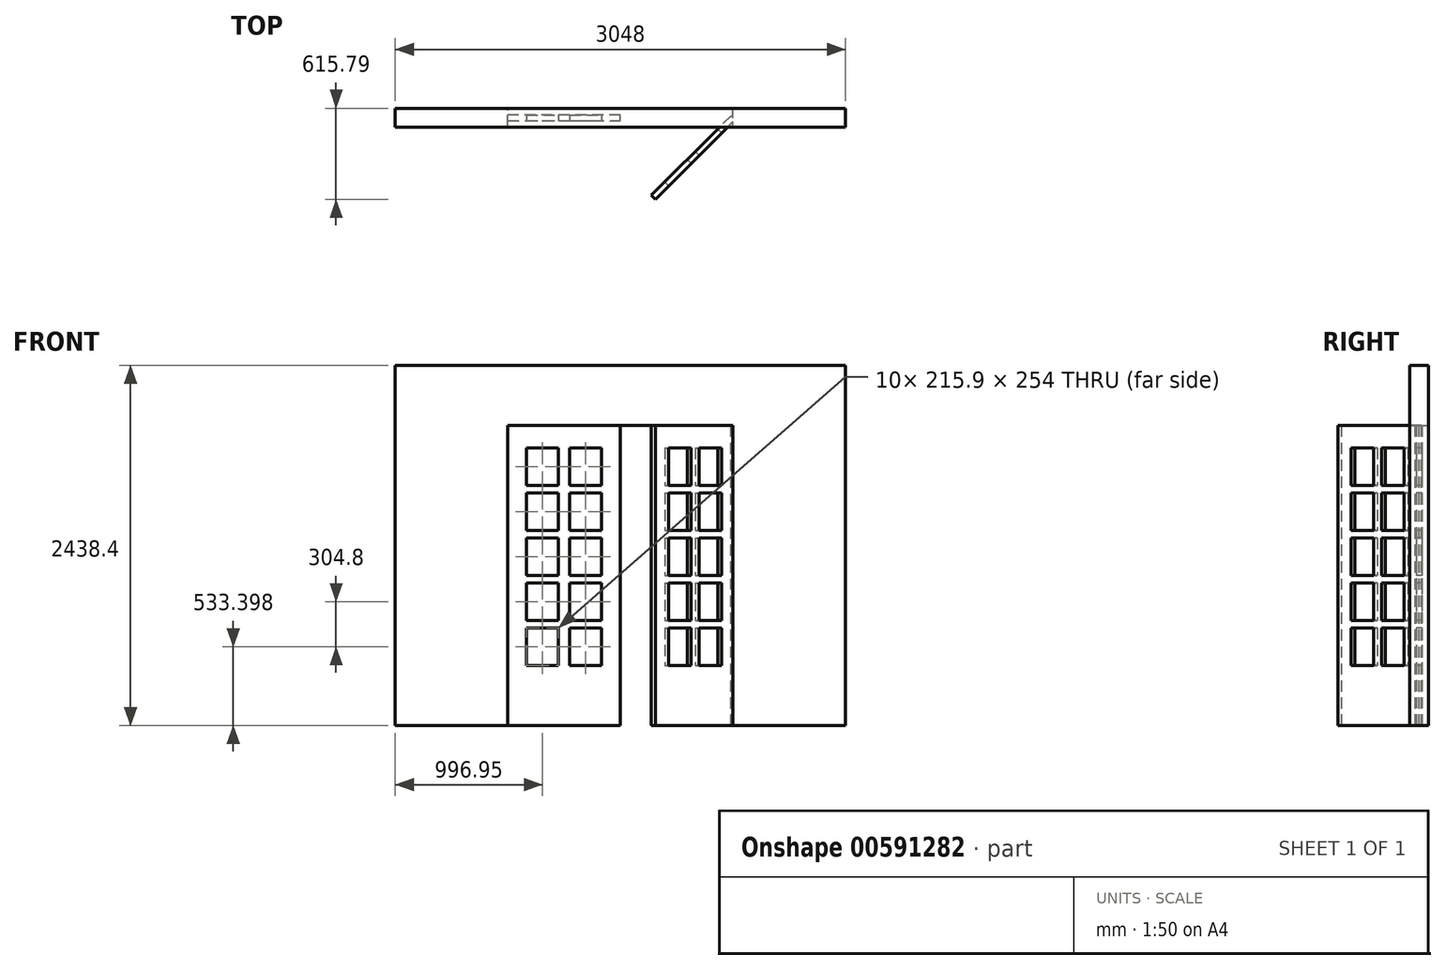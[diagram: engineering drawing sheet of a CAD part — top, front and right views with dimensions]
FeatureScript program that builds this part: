
annotation { "Feature Type Name" : "Feature", "Feature Type Description" : "" }
export const myFeature = defineFeature(function(context is Context, id is Id, definition is map)
    precondition{}
    {
        {
            var Q0;
            Q0=qCreatedBy(makeId("Front.planeOp"),FACE);
            var sketch = newSketch(context, id + "F0", { "sketchPlane" : qUnion([Q0])});
            skLineSegment(sketch, "E0", {"start": v(-2286, -766.6) * mm, "end": v(-1524, -766.6) * mm});
            skLineSegment(sketch, "E1", {"start": v(-1524, -766.6) * mm, "end": v(-1524, 1265.4) * mm});
            skLineSegment(sketch, "E2", {"start": v(-1524, 1265.4) * mm, "end": v(0, 1265.4) * mm});
            skLineSegment(sketch, "E3", {"start": v(0, 1265.4) * mm, "end": v(0, -766.6) * mm});
            skLineSegment(sketch, "E4", {"start": v(0, -766.6) * mm, "end": v(762, -766.6) * mm});
            skLineSegment(sketch, "E5", {"start": v(762, -766.6) * mm, "end": v(762, 1671.8) * mm});
            skLineSegment(sketch, "E6", {"start": v(762, 1671.8) * mm, "end": v(-2286, 1671.8) * mm});
            skLineSegment(sketch, "E7", {"start": v(-2286, 1671.8) * mm, "end": v(-2286, -766.6) * mm});
            skSolve(sketch);
        }
        {
            var Q0;
            Q0 = qSketchRegion(id + "F0", true);
            extrude(context, id + "F1", {"entities" : qUnion([Q0]), "depth" : 63.5 * mm, "offsetDistance" : 25.4 * mm, "hasSecondDirection" : true, "secondDirectionOppositeDirection" : true, "secondDirectionDepth" : 63.5 * mm});
        }
        {
            var Q0;
            Q0=qCreatedBy(makeId("Front.planeOp"),FACE);
            var sketch = newSketch(context, id + "F2", { "sketchPlane" : qUnion([Q0])});
            skLineSegment(sketch, "E8", {"start": v(-1524, -766.6) * mm, "end": v(-762, -766.6) * mm});
            skLineSegment(sketch, "E9", {"start": v(-762, -766.6) * mm, "end": v(-762, 1265.4) * mm});
            skLineSegment(sketch, "E10", {"start": v(-762, 1265.4) * mm, "end": v(-1524, 1265.4) * mm});
            skLineSegment(sketch, "E11", {"start": v(-1524, 1265.4) * mm, "end": v(-1524, -766.6) * mm});
            skSolve(sketch);
        }
        {
            var Q0;
            Q0 = qSketchRegion(id + "F2", true);
            extrude(context, id + "F3", {"entities" : qUnion([Q0]), "depth" : 19.05 * mm, "offsetDistance" : 25.4 * mm, "hasSecondDirection" : true, "secondDirectionOppositeDirection" : true, "secondDirectionDepth" : 19.05 * mm});
        }
        {
            var Q0;
            Q0=qCreatedBy(makeId("Right.planeOp"),FACE);
            var sketch = newSketch(context, id + "F4", { "sketchPlane" : qUnion([Q0])});
            skLineSegment(sketch, "E12", {"start": v(0, 83.42) * mm, "end": v(0, -71.8) * mm});
            skSolve(sketch);
        }
        {
            var Q0;
            Q0=qCreatedBy(makeId("Front.planeOp"),FACE);
            var Q1;
            Q1=sQuery(id+"F4.wireOp",EDGE,"E12");
            cPlane(context, id + "F5", {"entities" : qUnion([Q0, Q1]), "cplaneType" : CPlaneType.LINE_ANGLE, "offset" : 25.4 * mm, "angle" : 45 * degree, "oppositeDirection" : true, "width" : 152.4 * mm, "height" : 152.4 * mm});
        }
        {
            var Q0;
            Q0=makeQuery(id+"F3.opExtrude","CAP_FACE",FACE,{"disambiguationData":[OSD([sQuery(id+"F2.wireOp",EDGE,"E8"),sQuery(id+"F2.wireOp",EDGE,"E9"),sQuery(id+"F2.wireOp",EDGE,"E10"),sQuery(id+"F2.wireOp",EDGE,"E11")])],"isStart":false});
            var sketch = newSketch(context, id + "F6", { "sketchPlane" : qUnion([Q0])});
            skLineSegment(sketch, "E13.bottom", {"start": v(-1397, 1113) * mm, "end": v(-1181.1, 1113) * mm});
            skLineSegment(sketch, "E13.top", {"start": v(-1397, 859) * mm, "end": v(-1181.1, 859) * mm});
            skLineSegment(sketch, "E13.left", {"start": v(-1397, 1113) * mm, "end": v(-1397, 859) * mm});
            skLineSegment(sketch, "E13.right", {"start": v(-1181.1, 1113) * mm, "end": v(-1181.1, 859) * mm});
            skLineSegment(sketch, "E14.bottom", {"start": v(-1104.9, 1113) * mm, "end": v(-889, 1113) * mm});
            skLineSegment(sketch, "E14.top", {"start": v(-1104.9, 859) * mm, "end": v(-889, 859) * mm});
            skLineSegment(sketch, "E14.left", {"start": v(-1104.9, 1113) * mm, "end": v(-1104.9, 859) * mm});
            skLineSegment(sketch, "E14.right", {"start": v(-889, 1113) * mm, "end": v(-889, 859) * mm});
            skLineSegment(sketch, "E15.bottom", {"start": v(-1397, 808.2) * mm, "end": v(-1181.1, 808.2) * mm});
            skLineSegment(sketch, "E15.top", {"start": v(-1397, 554.2) * mm, "end": v(-1181.1, 554.2) * mm});
            skLineSegment(sketch, "E15.left", {"start": v(-1397, 808.2) * mm, "end": v(-1397, 554.2) * mm});
            skLineSegment(sketch, "E15.right", {"start": v(-1181.1, 808.2) * mm, "end": v(-1181.1, 554.2) * mm});
            skLineSegment(sketch, "E16.bottom", {"start": v(-1104.9, 808.2) * mm, "end": v(-889, 808.2) * mm});
            skLineSegment(sketch, "E16.top", {"start": v(-1104.9, 554.2) * mm, "end": v(-889, 554.2) * mm});
            skLineSegment(sketch, "E16.left", {"start": v(-1104.9, 808.2) * mm, "end": v(-1104.9, 554.2) * mm});
            skLineSegment(sketch, "E16.right", {"start": v(-889, 808.2) * mm, "end": v(-889, 554.2) * mm});
            skLineSegment(sketch, "E17.bottom", {"start": v(-1397, 503.4) * mm, "end": v(-1181.1, 503.4) * mm});
            skLineSegment(sketch, "E17.top", {"start": v(-1397, 249.4) * mm, "end": v(-1181.1, 249.4) * mm});
            skLineSegment(sketch, "E17.left", {"start": v(-1397, 503.4) * mm, "end": v(-1397, 249.4) * mm});
            skLineSegment(sketch, "E17.right", {"start": v(-1181.1, 503.4) * mm, "end": v(-1181.1, 249.4) * mm});
            skLineSegment(sketch, "E18.bottom", {"start": v(-1104.9, 503.4) * mm, "end": v(-889, 503.4) * mm});
            skLineSegment(sketch, "E18.top", {"start": v(-1104.9, 249.4) * mm, "end": v(-889, 249.4) * mm});
            skLineSegment(sketch, "E18.left", {"start": v(-1104.9, 503.4) * mm, "end": v(-1104.9, 249.4) * mm});
            skLineSegment(sketch, "E18.right", {"start": v(-889, 503.4) * mm, "end": v(-889, 249.4) * mm});
            skLineSegment(sketch, "E19.bottom", {"start": v(-1397, 198.6) * mm, "end": v(-1181.1, 198.6) * mm});
            skLineSegment(sketch, "E19.top", {"start": v(-1397, -55.4) * mm, "end": v(-1181.1, -55.4) * mm});
            skLineSegment(sketch, "E19.left", {"start": v(-1397, 198.6) * mm, "end": v(-1397, -55.4) * mm});
            skLineSegment(sketch, "E19.right", {"start": v(-1181.1, 198.6) * mm, "end": v(-1181.1, -55.4) * mm});
            skLineSegment(sketch, "E20.bottom", {"start": v(-1104.9, 198.6) * mm, "end": v(-889, 198.6) * mm});
            skLineSegment(sketch, "E20.top", {"start": v(-1104.9, -55.4) * mm, "end": v(-889, -55.4) * mm});
            skLineSegment(sketch, "E20.left", {"start": v(-1104.9, 198.6) * mm, "end": v(-1104.9, -55.4) * mm});
            skLineSegment(sketch, "E20.right", {"start": v(-889, 198.6) * mm, "end": v(-889, -55.4) * mm});
            skLineSegment(sketch, "E21.bottom", {"start": v(-1397, -106.2) * mm, "end": v(-1181.1, -106.2) * mm});
            skLineSegment(sketch, "E21.top", {"start": v(-1397, -360.2) * mm, "end": v(-1181.1, -360.2) * mm});
            skLineSegment(sketch, "E21.left", {"start": v(-1397, -106.2) * mm, "end": v(-1397, -360.2) * mm});
            skLineSegment(sketch, "E21.right", {"start": v(-1181.1, -106.2) * mm, "end": v(-1181.1, -360.2) * mm});
            skLineSegment(sketch, "E22.bottom", {"start": v(-1104.9, -106.2) * mm, "end": v(-889, -106.2) * mm});
            skLineSegment(sketch, "E22.top", {"start": v(-1104.9, -360.2) * mm, "end": v(-889, -360.2) * mm});
            skLineSegment(sketch, "E22.left", {"start": v(-1104.9, -106.2) * mm, "end": v(-1104.9, -360.2) * mm});
            skLineSegment(sketch, "E22.right", {"start": v(-889, -106.2) * mm, "end": v(-889, -360.2) * mm});
            skSolve(sketch);
        }
        {
            var Q0;
            Q0 = qSketchRegion(id + "F6", true);
            extrude(context, id + "F7", {"entities" : qUnion([Q0]), "operationType" : NewBodyOperationType.REMOVE, "endBound" : BoundingType.THROUGH_ALL, "oppositeDirection" : true, "depth" : 25.4 * mm, "offsetDistance" : 25.4 * mm});
        }
        {
            var Q0;
            Q0=qCreatedBy(id+"F5.planeOp",FACE);
            var sketch = newSketch(context, id + "F8", { "sketchPlane" : qUnion([Q0])});
            skLineSegment(sketch, "E23.bottom", {"start": v(0, -766.6) * mm, "end": v(762, -766.6) * mm});
            skLineSegment(sketch, "E23.top", {"start": v(0, 1265.4) * mm, "end": v(762, 1265.4) * mm});
            skLineSegment(sketch, "E23.left", {"start": v(0, -766.6) * mm, "end": v(0, 1265.4) * mm});
            skLineSegment(sketch, "E23.right", {"start": v(762, -766.6) * mm, "end": v(762, 1265.4) * mm});
            skLineSegment(sketch, "E24.bottom", {"start": v(635, -106.2) * mm, "end": v(419.1, -106.2) * mm});
            skLineSegment(sketch, "E24.top", {"start": v(635, -360.2) * mm, "end": v(419.1, -360.2) * mm});
            skLineSegment(sketch, "E24.left", {"start": v(635, -106.2) * mm, "end": v(635, -360.2) * mm});
            skLineSegment(sketch, "E24.right", {"start": v(419.1, -106.2) * mm, "end": v(419.1, -360.2) * mm});
            skLineSegment(sketch, "E25.bottom", {"start": v(342.9, -106.2) * mm, "end": v(127, -106.2) * mm});
            skLineSegment(sketch, "E25.top", {"start": v(342.9, -360.2) * mm, "end": v(127, -360.2) * mm});
            skLineSegment(sketch, "E25.left", {"start": v(342.9, -106.2) * mm, "end": v(342.9, -360.2) * mm});
            skLineSegment(sketch, "E25.right", {"start": v(127, -106.2) * mm, "end": v(127, -360.2) * mm});
            skLineSegment(sketch, "E26.bottom", {"start": v(635, 198.6) * mm, "end": v(419.1, 198.6) * mm});
            skLineSegment(sketch, "E26.top", {"start": v(635, -55.4) * mm, "end": v(419.1, -55.4) * mm});
            skLineSegment(sketch, "E26.left", {"start": v(635, 198.6) * mm, "end": v(635, -55.4) * mm});
            skLineSegment(sketch, "E26.right", {"start": v(419.1, 198.6) * mm, "end": v(419.1, -55.4) * mm});
            skLineSegment(sketch, "E27.bottom", {"start": v(342.9, 198.6) * mm, "end": v(127, 198.6) * mm});
            skLineSegment(sketch, "E27.top", {"start": v(342.9, -55.4) * mm, "end": v(127, -55.4) * mm});
            skLineSegment(sketch, "E27.left", {"start": v(342.9, 198.6) * mm, "end": v(342.9, -55.4) * mm});
            skLineSegment(sketch, "E27.right", {"start": v(127, 198.6) * mm, "end": v(127, -55.4) * mm});
            skLineSegment(sketch, "E28.bottom", {"start": v(635, 503.4) * mm, "end": v(419.1, 503.4) * mm});
            skLineSegment(sketch, "E28.top", {"start": v(635, 249.4) * mm, "end": v(419.1, 249.4) * mm});
            skLineSegment(sketch, "E28.left", {"start": v(635, 503.4) * mm, "end": v(635, 249.4) * mm});
            skLineSegment(sketch, "E28.right", {"start": v(419.1, 503.4) * mm, "end": v(419.1, 249.4) * mm});
            skLineSegment(sketch, "E29.bottom", {"start": v(342.9, 503.4) * mm, "end": v(127, 503.4) * mm});
            skLineSegment(sketch, "E29.top", {"start": v(342.9, 249.4) * mm, "end": v(127, 249.4) * mm});
            skLineSegment(sketch, "E29.left", {"start": v(342.9, 503.4) * mm, "end": v(342.9, 249.4) * mm});
            skLineSegment(sketch, "E29.right", {"start": v(127, 503.4) * mm, "end": v(127, 249.4) * mm});
            skLineSegment(sketch, "E30.bottom", {"start": v(635, 808.2) * mm, "end": v(419.1, 808.2) * mm});
            skLineSegment(sketch, "E30.top", {"start": v(635, 554.2) * mm, "end": v(419.1, 554.2) * mm});
            skLineSegment(sketch, "E30.left", {"start": v(635, 808.2) * mm, "end": v(635, 554.2) * mm});
            skLineSegment(sketch, "E30.right", {"start": v(419.1, 808.2) * mm, "end": v(419.1, 554.2) * mm});
            skLineSegment(sketch, "E31.bottom", {"start": v(342.9, 808.2) * mm, "end": v(127, 808.2) * mm});
            skLineSegment(sketch, "E31.top", {"start": v(342.9, 554.2) * mm, "end": v(127, 554.2) * mm});
            skLineSegment(sketch, "E31.left", {"start": v(342.9, 808.2) * mm, "end": v(342.9, 554.2) * mm});
            skLineSegment(sketch, "E31.right", {"start": v(127, 808.2) * mm, "end": v(127, 554.2) * mm});
            skLineSegment(sketch, "E32.bottom", {"start": v(635, 1113) * mm, "end": v(419.1, 1113) * mm});
            skLineSegment(sketch, "E32.top", {"start": v(635, 859) * mm, "end": v(419.1, 859) * mm});
            skLineSegment(sketch, "E32.left", {"start": v(635, 1113) * mm, "end": v(635, 859) * mm});
            skLineSegment(sketch, "E32.right", {"start": v(419.1, 1113) * mm, "end": v(419.1, 859) * mm});
            skLineSegment(sketch, "E33.bottom", {"start": v(342.9, 1113) * mm, "end": v(127, 1113) * mm});
            skLineSegment(sketch, "E33.top", {"start": v(342.9, 859) * mm, "end": v(127, 859) * mm});
            skLineSegment(sketch, "E33.left", {"start": v(342.9, 1113) * mm, "end": v(342.9, 859) * mm});
            skLineSegment(sketch, "E33.right", {"start": v(127, 1113) * mm, "end": v(127, 859) * mm});
            skSolve(sketch);
        }
        {
            var Q0;
            Q0 = qSketchRegion(id + "F8", true);
            extrude(context, id + "F9", {"entities" : qUnion([Q0]), "operationType" : NewBodyOperationType.ADD, "depth" : 19.05 * mm, "offsetDistance" : 25.4 * mm, "hasSecondDirection" : true, "secondDirectionOppositeDirection" : true, "secondDirectionDepth" : 19.05 * mm});
        }
    });
